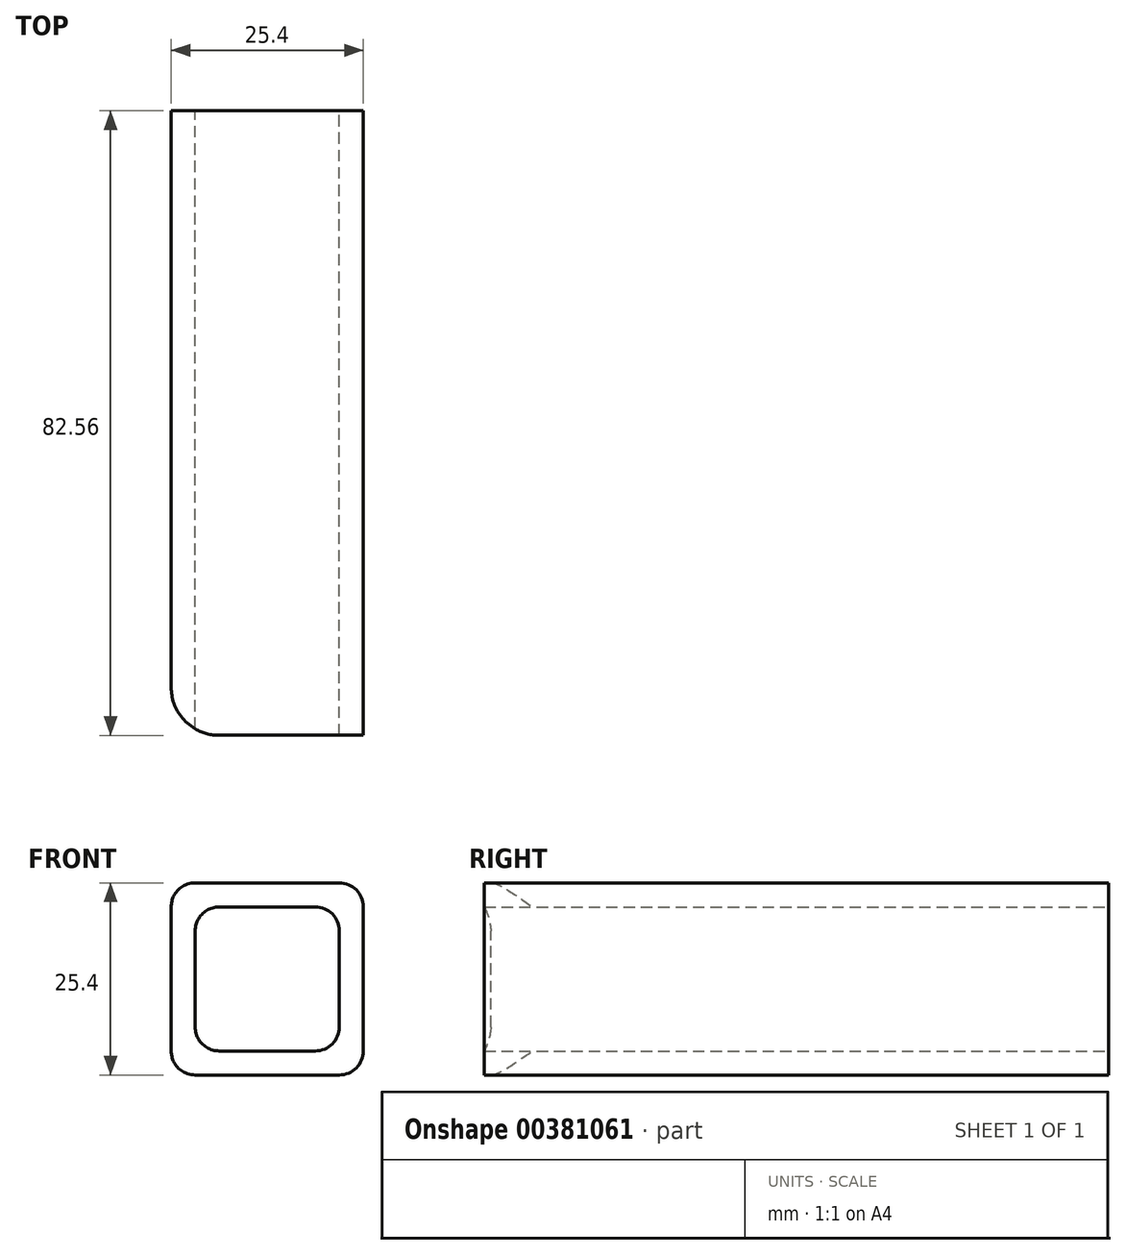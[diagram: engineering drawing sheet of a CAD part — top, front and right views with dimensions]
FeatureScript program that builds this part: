
annotation { "Feature Type Name" : "Feature", "Feature Type Description" : "" }
export const myFeature = defineFeature(function(context is Context, id is Id, definition is map)
    precondition{}
    {
        {
            var Q0;
            Q0=qCreatedBy(makeId("Front.planeOp"),FACE);
            var sketch = newSketch(context, id + "F0", { "sketchPlane" : qUnion([Q0])});
            skLineSegment(sketch, "E0.bottom", {"start": v(9.52, 12.7) * mm, "end": v(-9.53, 12.7) * mm});
            skLineSegment(sketch, "E0.top", {"start": v(9.53, -12.7) * mm, "end": v(-9.52, -12.7) * mm});
            skLineSegment(sketch, "E0.left", {"start": v(12.7, 9.53) * mm, "end": v(12.7, -9.52) * mm});
            skLineSegment(sketch, "E0.right", {"start": v(-12.7, 9.53) * mm, "end": v(-12.7, -9.52) * mm});
            skPoint(sketch, "E0.middle", {"position": v(0, 0) * mm});
            skLineSegment(sketch, "E1.bottom", {"start": v(6.35, 9.53) * mm, "end": v(-6.35, 9.53) * mm});
            skLineSegment(sketch, "E1.top", {"start": v(6.35, -9.53) * mm, "end": v(-6.35, -9.53) * mm});
            skLineSegment(sketch, "E1.left", {"start": v(9.53, 6.35) * mm, "end": v(9.53, -6.35) * mm});
            skLineSegment(sketch, "E1.right", {"start": v(-9.53, 6.35) * mm, "end": v(-9.53, -6.35) * mm});
            skPoint(sketch, "E2.visualSharp", {"position": v(-9.53, 9.53) * mm});
            skArc(sketch, "E2.filletArc", {"start": v(-6.35, 9.52) * mm, "mid": v(-8.6, 8.6) * mm, "end": v(-9.53, 6.35) * mm});
            skPoint(sketch, "E3.visualSharp", {"position": v(9.53, 9.53) * mm});
            skArc(sketch, "E3.filletArc", {"start": v(9.53, 6.35) * mm, "mid": v(8.6, 8.6) * mm, "end": v(6.35, 9.53) * mm});
            skPoint(sketch, "E4.visualSharp", {"position": v(9.53, -9.53) * mm});
            skArc(sketch, "E4.filletArc", {"start": v(6.35, -9.53) * mm, "mid": v(8.6, -8.6) * mm, "end": v(9.53, -6.35) * mm});
            skPoint(sketch, "E5.visualSharp", {"position": v(-9.53, -9.53) * mm});
            skArc(sketch, "E5.filletArc", {"start": v(-9.53, -6.35) * mm, "mid": v(-8.6, -8.6) * mm, "end": v(-6.35, -9.53) * mm});
            skPoint(sketch, "E6.visualSharp", {"position": v(12.7, -12.7) * mm});
            skArc(sketch, "E6.filletArc", {"start": v(9.53, -12.7) * mm, "mid": v(11.77, -11.77) * mm, "end": v(12.7, -9.52) * mm});
            skPoint(sketch, "E7.visualSharp", {"position": v(12.7, 12.7) * mm});
            skArc(sketch, "E7.filletArc", {"start": v(12.7, 9.53) * mm, "mid": v(11.77, 11.77) * mm, "end": v(9.52, 12.7) * mm});
            skPoint(sketch, "E8.visualSharp", {"position": v(-12.7, 12.7) * mm});
            skArc(sketch, "E8.filletArc", {"start": v(-9.53, 12.7) * mm, "mid": v(-11.77, 11.77) * mm, "end": v(-12.7, 9.53) * mm});
            skPoint(sketch, "E9.visualSharp", {"position": v(-12.7, -12.7) * mm});
            skArc(sketch, "E9.filletArc", {"start": v(-12.7, -9.52) * mm, "mid": v(-11.77, -11.77) * mm, "end": v(-9.52, -12.7) * mm});
            skSolve(sketch);
        }
        {
            var Q0;
            Q0=makeQuery(id+"F0.imprint","IMPRINT",FACE,{"disambiguationData":[TD([[makeQuery(id+"F0.imprint","IMPRINT",EDGE,{"derivedFrom":sQuery(id+"F0.wireOp",EDGE,"E0.bottom")}),1.0]])]});
            extrude(context, id + "F1", {"entities" : qUnion([Q0]), "depth" : 82.55 * mm, "symmetric" : true});
        }
        {
            var Q0;
            Q0=makeQuery(id+"F1.opExtrude","CAP_EDGE",EDGE,{"disambiguationData":[OSD([sQuery(id+"F0.wireOp",EDGE,"E0.right")])],"isStart":false});
            fillet(context, id + "F2", {"entities" : qUnion([Q0]), "radius" : 6.35 * mm, "allowEdgeOverflow" : false});
        }
    });
